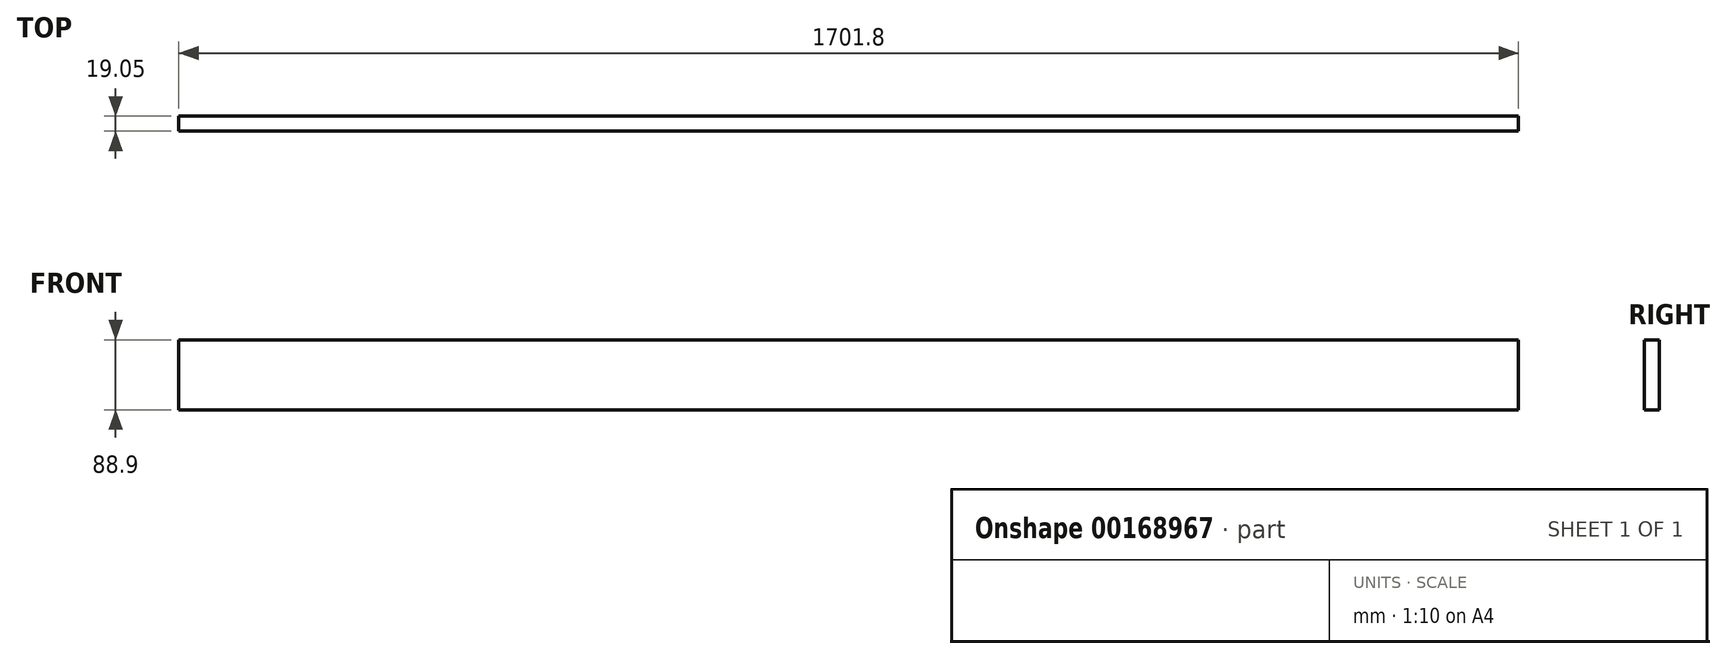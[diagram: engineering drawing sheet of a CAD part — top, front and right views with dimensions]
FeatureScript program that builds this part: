
annotation { "Feature Type Name" : "Feature", "Feature Type Description" : "" }
export const myFeature = defineFeature(function(context is Context, id is Id, definition is map)
    precondition{}
    {
        {
            var Q0;
            Q0=qCreatedBy(makeId("Front.planeOp"),FACE);
            var sketch = newSketch(context, id + "F0", { "sketchPlane" : qUnion([Q0])});
            skLineSegment(sketch, "E0.bottom", {"start": v(843.86, -23.37) * mm, "end": v(-857.94, -23.37) * mm});
            skLineSegment(sketch, "E0.top", {"start": v(843.86, -112.27) * mm, "end": v(-857.94, -112.27) * mm});
            skLineSegment(sketch, "E0.left", {"start": v(843.86, -23.37) * mm, "end": v(843.86, -112.27) * mm});
            skLineSegment(sketch, "E0.right", {"start": v(-857.94, -23.37) * mm, "end": v(-857.94, -112.27) * mm});
            skSolve(sketch);
        }
        {
            var Q0;
            Q0 = qSketchRegion(id + "F0", true);
            extrude(context, id + "F1", {"entities" : qUnion([Q0]), "depth" : 19.05 * mm});
        }
    });
